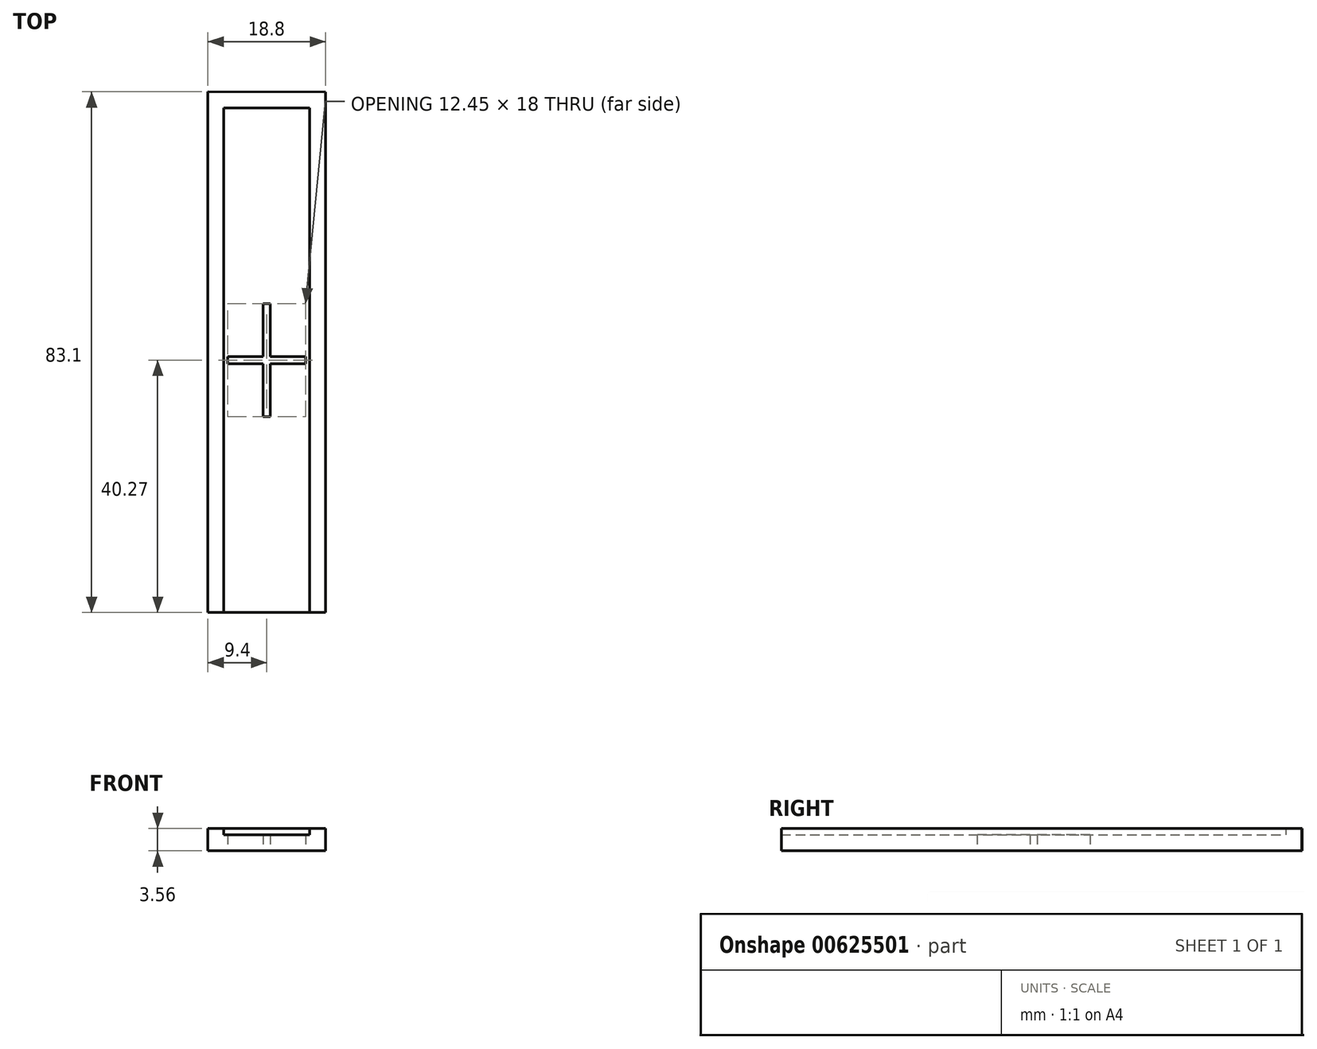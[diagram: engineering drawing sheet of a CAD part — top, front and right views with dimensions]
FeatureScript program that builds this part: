
annotation { "Feature Type Name" : "Feature", "Feature Type Description" : "" }
export const myFeature = defineFeature(function(context is Context, id is Id, definition is map)
    precondition{}
    {
        {
            var Q0;
            Q0=qCreatedBy(makeId("Top.planeOp"),FACE);
            var sketch = newSketch(context, id + "F0", { "sketchPlane" : qUnion([Q0])});
            skLineSegment(sketch, "E0.bottom", {"start": v(6.86, -40.27) * mm, "end": v(-6.86, -40.27) * mm});
            skLineSegment(sketch, "E0.top", {"start": v(6.86, 40.27) * mm, "end": v(-6.86, 40.27) * mm});
            skLineSegment(sketch, "E0.left", {"start": v(6.86, -40.27) * mm, "end": v(6.86, 40.27) * mm});
            skLineSegment(sketch, "E0.right", {"start": v(-6.86, -40.27) * mm, "end": v(-6.86, 40.27) * mm});
            skPoint(sketch, "E0.middle", {"position": v(0, 0) * mm});
            skLineSegment(sketch, "E1.bottom", {"start": v(0.57, 9) * mm, "end": v(-0.57, 9) * mm});
            skLineSegment(sketch, "E1.top", {"start": v(0.57, -9) * mm, "end": v(-0.57, -9) * mm});
            skLineSegment(sketch, "E1.left", {"start": v(0.57, 9) * mm, "end": v(0.57, 0.57) * mm});
            skLineSegment(sketch, "E1.right", {"start": v(-0.57, 9) * mm, "end": v(-0.57, 0.57) * mm});
            skLineSegment(sketch, "E2.bottom", {"start": v(6.22, -0.57) * mm, "end": v(0.57, -0.57) * mm});
            skLineSegment(sketch, "E2.top", {"start": v(6.22, 0.57) * mm, "end": v(0.57, 0.57) * mm});
            skLineSegment(sketch, "E2.left", {"start": v(6.22, -0.57) * mm, "end": v(6.22, 0.57) * mm});
            skLineSegment(sketch, "E2.right", {"start": v(-6.22, -0.57) * mm, "end": v(-6.22, 0.57) * mm});
            skLineSegment(sketch, "E3.trimOffspring", {"start": v(-0.57, -0.57) * mm, "end": v(-0.57, -9) * mm});
            skLineSegment(sketch, "E4.trimOffspring", {"start": v(-0.57, 0.57) * mm, "end": v(-6.22, 0.57) * mm});
            skLineSegment(sketch, "E5.trimOffspring", {"start": v(0.57, -0.57) * mm, "end": v(0.57, -9) * mm});
            skLineSegment(sketch, "E6.trimOffspring", {"start": v(-0.57, -0.57) * mm, "end": v(-6.22, -0.57) * mm});
            skPoint(sketch, "E7.end.orphan", {"position": v(-9.4, -40.27) * mm});
            skPoint(sketch, "E8.start.orphan", {"position": v(9.4, -40.27) * mm});
            skLineSegment(sketch, "E9", {"start": v(-9.4, 42.83) * mm, "end": v(-9.4, -40.27) * mm});
            skLineSegment(sketch, "E10", {"start": v(6.86, -40.27) * mm, "end": v(9.4, -40.27) * mm});
            skLineSegment(sketch, "E11", {"start": v(9.4, -40.27) * mm, "end": v(9.4, 42.8) * mm});
            skLineSegment(sketch, "E12", {"start": v(9.4, 42.8) * mm, "end": v(-9.4, 42.83) * mm});
            skLineSegment(sketch, "E13", {"start": v(-9.4, -40.27) * mm, "end": v(-6.86, -40.27) * mm});
            skSolve(sketch);
        }
        {
            var Q0;
            Q0=makeQuery(id+"F0.imprint","IMPRINT",FACE,{"disambiguationData":[TD([[makeQuery(id+"F0.imprint","IMPRINT",EDGE,{"derivedFrom":sQuery(id+"F0.wireOp",EDGE,"E0.bottom")}),-1.0]])]});
            extrude(context, id + "F1", {"entities" : qUnion([Q0]), "flatOperationType" : FlatOperationType.REMOVE, "depth" : 2.54 * mm, "offsetDistance" : 25.4 * mm, "domain" : OperationDomain.MODEL});
        }
        {
            var Q0;
            Q0=makeQuery(id+"F0.imprint","IMPRINT",FACE,{"disambiguationData":[TD([[makeQuery(id+"F0.imprint","IMPRINT",EDGE,{"derivedFrom":sQuery(id+"F0.wireOp",EDGE,"E0.top")}),-1.0]])]});
            extrude(context, id + "F2", {"entities" : qUnion([Q0]), "operationType" : NewBodyOperationType.ADD, "depth" : 3.56 * mm, "offsetDistance" : 25.4 * mm});
        }
    });
